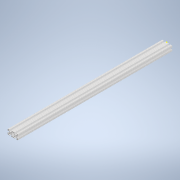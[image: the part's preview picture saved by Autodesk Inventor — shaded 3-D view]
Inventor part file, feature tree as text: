
AUTODESK INVENTOR PART (.ipt)
format: ipt  version: 2020 (Build 240168000, 168)  size: 332,800 bytes
history: native  units: in
note: dims shown in document units (in); Inventor stores cm internally (conversion verified against a paired STEP export)
features: sketch x2, extrude x1
ambient origin geometry x8: Origin, YZ Plane, XZ Plane, XY Plane, X Axis, Y Axis, Z Axis, Center Point
bodies: Solid1 (feature_tree)
feature tree (3):
  extrude  "Extrusion1"  [1 undecoded]
  sketch  "Sketch2"
  sketch  "Sketch1"  dims[d0=30.0in d1=0.0in]
note: 1 required parameter value undecoded (feature->parameter linkage not recoverable at this tier; creation-order binding heuristic only, values carry confidence <= 0.55)
